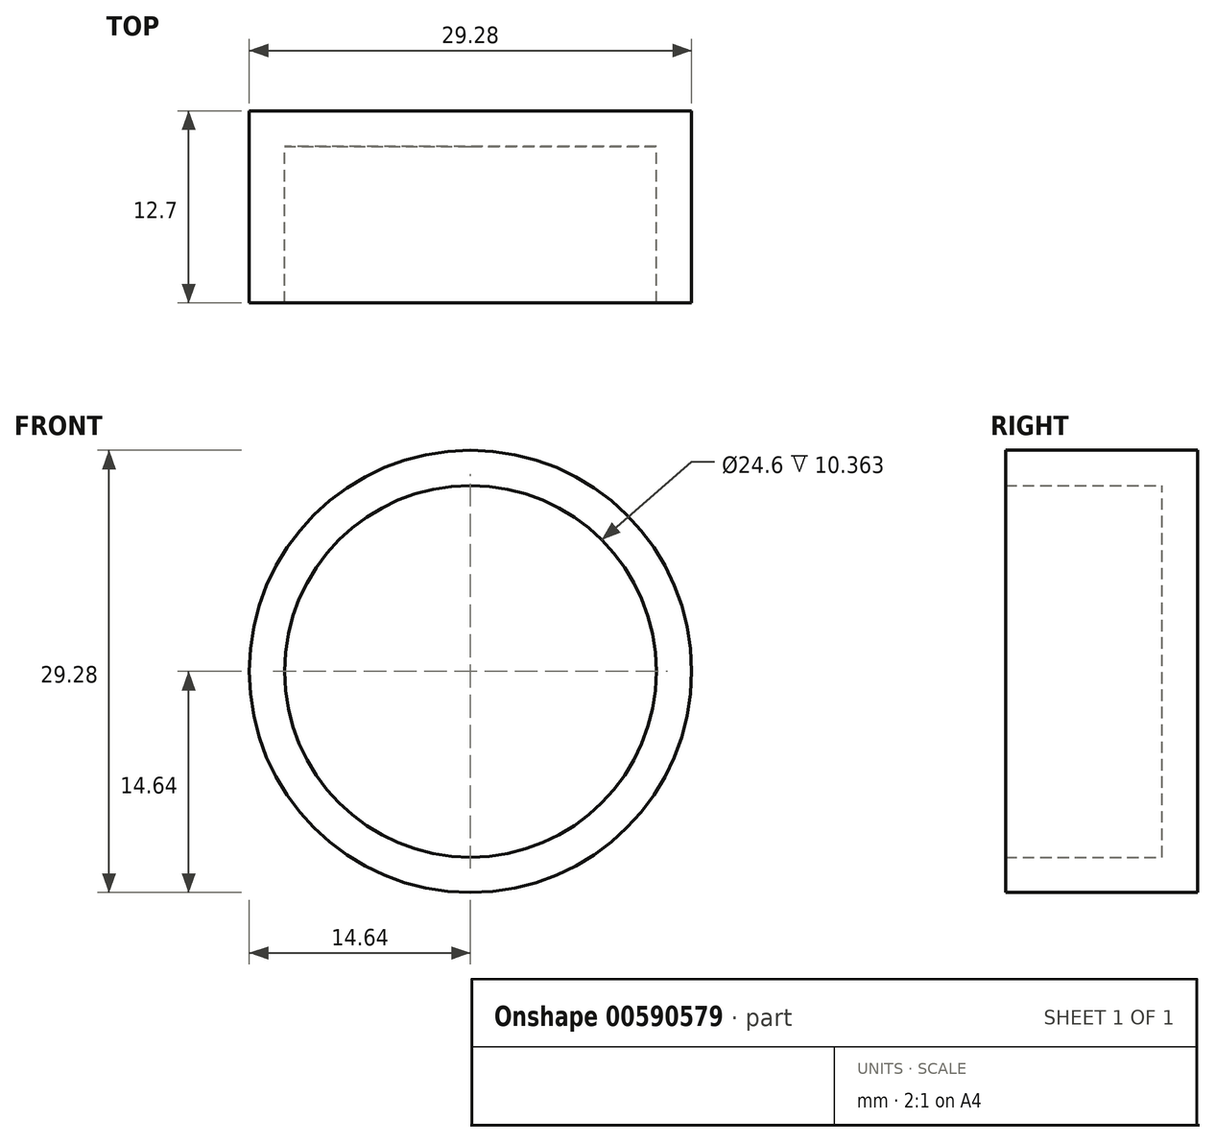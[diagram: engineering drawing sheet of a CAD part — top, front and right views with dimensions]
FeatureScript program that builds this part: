
annotation { "Feature Type Name" : "Feature", "Feature Type Description" : "" }
export const myFeature = defineFeature(function(context is Context, id is Id, definition is map)
    precondition{}
    {
        {
            var Q0;
            Q0=qCreatedBy(makeId("Front.planeOp"),FACE);
            var sketch = newSketch(context, id + "F0", { "sketchPlane" : qUnion([Q0])});
            skCircle(sketch, "E0", {"center": v(0, 0) * mm, "radius": 14.64 * mm});
            skSolve(sketch);
        }
        {
            var Q0;
            Q0=makeQuery(id+"F0.imprint","IMPRINT",FACE,{"disambiguationData":[TD([[makeQuery(id+"F0.imprint","IMPRINT",EDGE,{"derivedFrom":sQuery(id+"F0.wireOp",EDGE,"E0")}),1.0]])]});
            extrude(context, id + "F1", {"entities" : qUnion([Q0]), "depth" : 12.7 * mm, "offsetDistance" : 25.4 * mm});
        }
        {
            var Q0;
            Q0=makeQuery(id+"F1.opExtrude","CAP_FACE",FACE,{"disambiguationData":[OSD([sQuery(id+"F0.wireOp",EDGE,"E0")])],"isStart":false});
            shell(context, id + "F2", {"entities" : qUnion([Q0]), "thickness" : 2.34 * mm});
        }
    });
